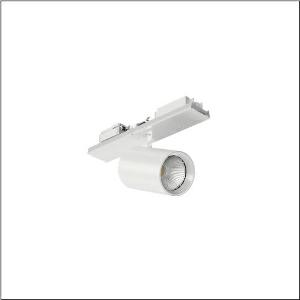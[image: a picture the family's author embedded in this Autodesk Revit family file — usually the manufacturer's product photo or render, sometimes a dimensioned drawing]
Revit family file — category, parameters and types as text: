
# Revit family: licross_r__spot_31_51sl13da45b_aeee
name_source: partatom
category: Lighting Fixtures
units: mm (PartAtom-declared; Revit-internal decimal feet)

## family parameters
Cut with Voids When Loaded = No
Host = Face
Light Source = No
Part Type = Normal
Room Calculation Point = No
Round Connector Dimension = Use Diameter
Shared = No

## types (1)
- --- (1 x LED, 5190 lm, 43.9 W, 4000K)
    Apparent Load = 44 VA
    CIE Flux Codes = 92 97 99 100 100
    Color Rendering = 90
    Color Temperature = 4000K
    Default Elevation = 1800 mm
    Description = Licross® Spot 31, directional spotlight, light control with lens, of plastic, LED rated luminous flux: 5.190lm, light colour: 940, with plug, 5-pole, mains connection: 220..240V, AC, 50/60Hz, of aluminium, traffic white (RAL 9016), length: 300mm, diameter: 90mm, protection rating (complete): IP20, insulation class (complete): insulation class I (protective earthing), certification: CE, packaging unit: 1 piece
    Height = 175 mm
    Lamp = 1 x LED
    Lamp Light Flux = 5190 lm
    Lamp Power = 43.9 W
    Lamp count = 1
    Length = 90 mm
    Luminous efficacy = 118 lm/W
    Manufacturer = Siteco
    ModVariant = No
    Model = 51SL13DA45B
    Mounting Place = Ceiling
    Mounting Type = Pendant
    Number of Poles = 1
    OnlyDefault = Yes
    Power Factor = 1
    Product Name = Licross® Spot 31
    Product group = directional spotlight
    ProductGroupID = 905
    Protection Class = Protection class I
    Protection Degree = IP 20
    RLX_Detail_Level = 1
    RLX_Emergency_Light_Flux = 0 lm
    RLX_Emergency_Type = 0
    RLX_Emergency_Type_DB = No
    RlxData = <blob elided: 14789 chars, md5=5ea4c497>
    Socket = socket
    Standby Power = 0 W
    System Light Flux = 5190 lm
    System Power = 44 W
    Type Comments = factory setting: luminous flux: 100 % | (ON | ON | ON) | 1050 mA
    Type Image = l_1245720.jpg
    URL = http://relux.com
    VarID = @adj_102291
    Voltage = 0 V
    Weight = 0.00 kg
    Width = 0 mm  [stored 0 ft]

note: [stored X ft] marks values corroborated as IEEE doubles in the binary element streams (Revit-internal decimal feet)

## geometry (parser evidence)
native form markers: Sweep x10
no freeform markers — native parametric forms only
